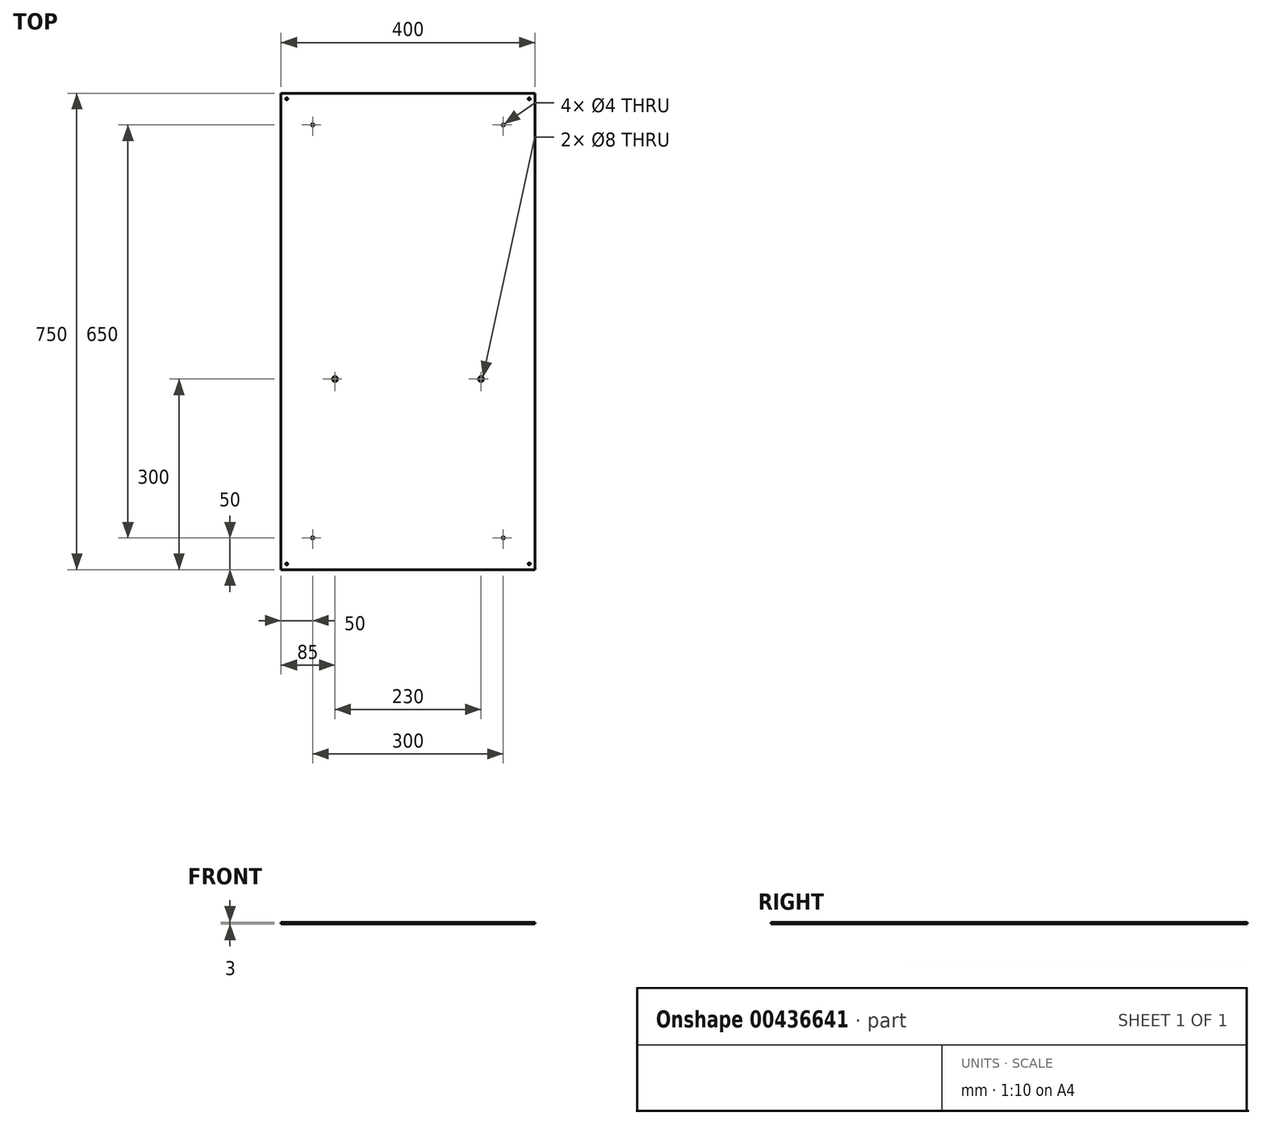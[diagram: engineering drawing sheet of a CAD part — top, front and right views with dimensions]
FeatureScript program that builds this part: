
annotation { "Feature Type Name" : "Feature", "Feature Type Description" : "" }
export const myFeature = defineFeature(function(context is Context, id is Id, definition is map)
    precondition{}
    {
        {
            var Q0;
            Q0=qCreatedBy(makeId("Top.planeOp"),FACE);
            var sketch = newSketch(context, id + "F0", { "sketchPlane" : qUnion([Q0])});
            skLineSegment(sketch, "E0.bottom", {"start": v(200, 375) * mm, "end": v(-200, 375) * mm});
            skLineSegment(sketch, "E0.top", {"start": v(200, -375) * mm, "end": v(-200, -375) * mm});
            skLineSegment(sketch, "E0.left", {"start": v(200, 375) * mm, "end": v(200, -375) * mm});
            skLineSegment(sketch, "E0.right", {"start": v(-200, 375) * mm, "end": v(-200, -375) * mm});
            skPoint(sketch, "E0.middle", {"position": v(0, 0) * mm});
            skLineSegment(sketch, "E1", {"start": v(-191, 375) * mm, "end": v(-191, 366) * mm, "construction": true});
            skLineSegment(sketch, "E2", {"start": v(-191, 366) * mm, "end": v(-200, 366) * mm, "construction": true});
            skCircle(sketch, "E3", {"center": v(-191, 366) * mm, "radius": 1.7 * mm});
            skLineSegment(sketch, "E4", {"start": v(191, 375) * mm, "end": v(191, 366) * mm, "construction": true});
            skLineSegment(sketch, "E5", {"start": v(191, 366) * mm, "end": v(200, 366) * mm, "construction": true});
            skCircle(sketch, "E6", {"center": v(191, 366) * mm, "radius": 1.7 * mm});
            skLineSegment(sketch, "E7", {"start": v(-200, -366) * mm, "end": v(-191, -366) * mm, "construction": true});
            skLineSegment(sketch, "E8", {"start": v(-191, -366) * mm, "end": v(-191, -375) * mm, "construction": true});
            skCircle(sketch, "E9", {"center": v(-191, -366) * mm, "radius": 1.7 * mm});
            skLineSegment(sketch, "E10", {"start": v(200, -366) * mm, "end": v(191, -366) * mm, "construction": true});
            skLineSegment(sketch, "E11", {"start": v(191, -366) * mm, "end": v(191, -375) * mm, "construction": true});
            skCircle(sketch, "E12", {"center": v(191, -366) * mm, "radius": 1.7 * mm});
            skLineSegment(sketch, "E13", {"start": v(-150, 375) * mm, "end": v(-150, 325) * mm, "construction": true});
            skLineSegment(sketch, "E14", {"start": v(-150, 325) * mm, "end": v(-200, 325) * mm, "construction": true});
            skCircle(sketch, "E15", {"center": v(-150, 325) * mm, "radius": 2 * mm});
            skLineSegment(sketch, "E16", {"start": v(200, 325) * mm, "end": v(150, 325) * mm, "construction": true});
            skLineSegment(sketch, "E17", {"start": v(150, 325) * mm, "end": v(150, 375) * mm, "construction": true});
            skCircle(sketch, "E18", {"center": v(150, 325) * mm, "radius": 2 * mm});
            skLineSegment(sketch, "E19", {"start": v(-150, -375) * mm, "end": v(-150, -325) * mm, "construction": true});
            skLineSegment(sketch, "E20", {"start": v(-150, -325) * mm, "end": v(-200, -325) * mm, "construction": true});
            skCircle(sketch, "E21", {"center": v(-150, -325) * mm, "radius": 2 * mm});
            skLineSegment(sketch, "E22", {"start": v(150, -375) * mm, "end": v(150, -325) * mm, "construction": true});
            skLineSegment(sketch, "E23", {"start": v(150, -325) * mm, "end": v(200, -325) * mm, "construction": true});
            skCircle(sketch, "E24", {"center": v(150, -325) * mm, "radius": 2 * mm});
            skLineSegment(sketch, "E25", {"start": v(0, -75) * mm, "end": v(0, 0) * mm, "construction": true});
            skLineSegment(sketch, "E26", {"start": v(0, -75) * mm, "end": v(115, -75) * mm, "construction": true});
            skLineSegment(sketch, "E27", {"start": v(0, -75) * mm, "end": v(-115, -75) * mm, "construction": true});
            skCircle(sketch, "E28", {"center": v(115, -75) * mm, "radius": 4 * mm});
            skCircle(sketch, "E29", {"center": v(-115, -75) * mm, "radius": 4 * mm});
            skSolve(sketch);
        }
        {
            var Q0;
            Q0=makeQuery(id+"F0.imprint","IMPRINT",FACE,{"disambiguationData":[TD([[makeQuery(id+"F0.imprint","IMPRINT",EDGE,{"derivedFrom":sQuery(id+"F0.wireOp",EDGE,"E0.bottom")}),1.0]])]});
            extrude(context, id + "F1", {"entities" : qUnion([Q0]), "depth" : 3 * mm});
        }
    });
